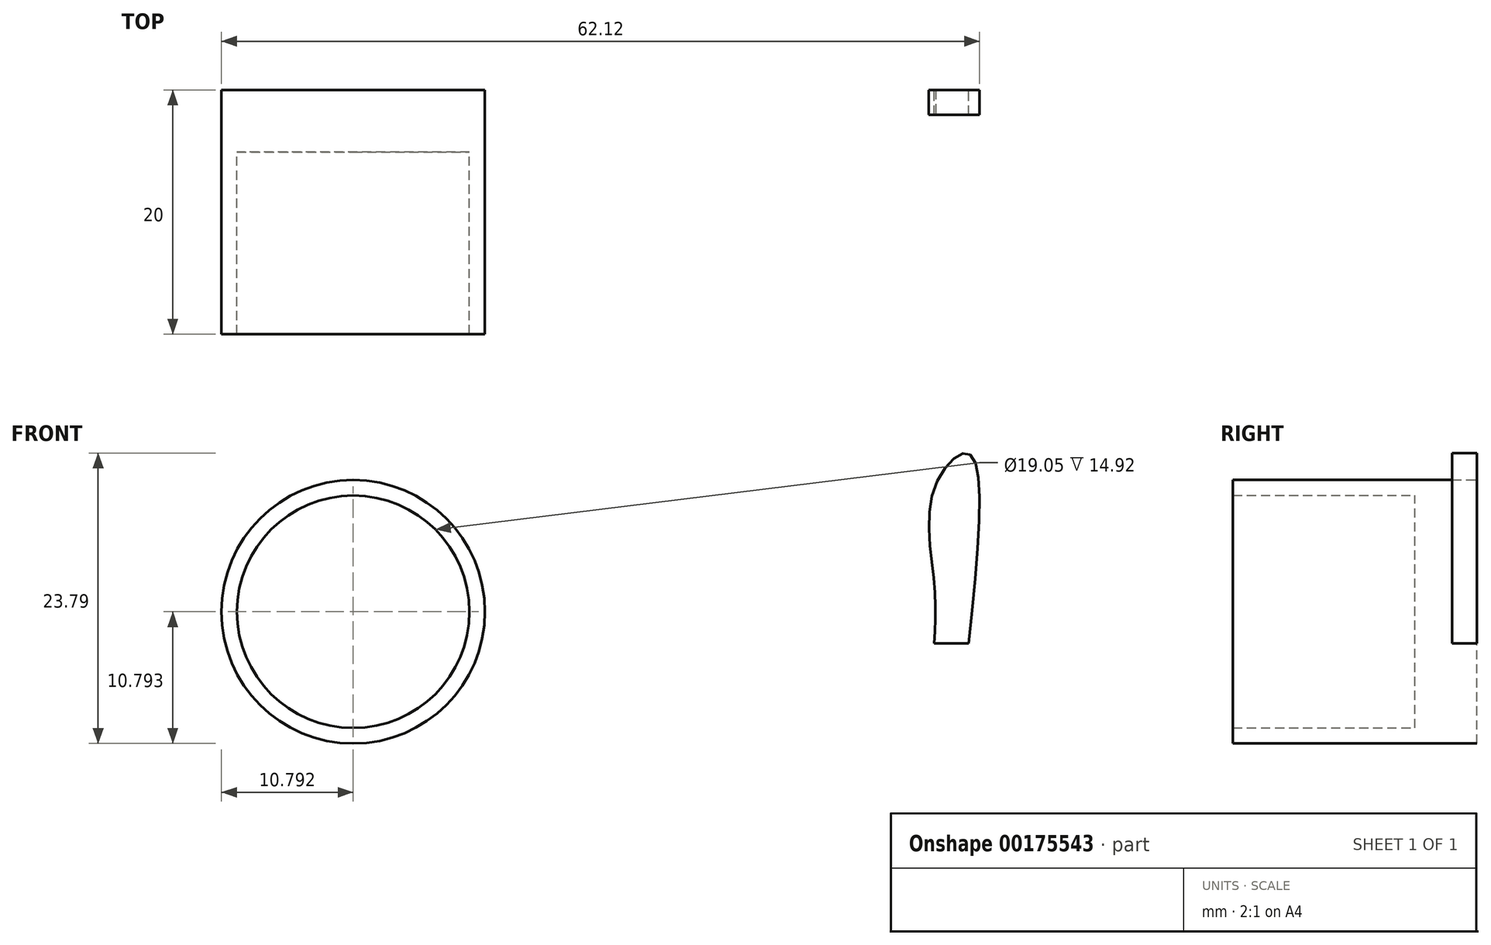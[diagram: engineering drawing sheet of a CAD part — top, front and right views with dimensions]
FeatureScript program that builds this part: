
annotation { "Feature Type Name" : "Feature", "Feature Type Description" : "" }
export const myFeature = defineFeature(function(context is Context, id is Id, definition is map)
    precondition{}
    {
        {
            var Q0;
            Q0=qCreatedBy(makeId("Front.planeOp"),FACE);
            var sketch = newSketch(context, id + "F0", { "sketchPlane" : qUnion([Q0])});
            skCircle(sketch, "E0", {"center": v(-33.09, 15.7) * mm, "radius": 10.8 * mm});
            skCircle(sketch, "E1", {"center": v(-33.09, 15.7) * mm, "radius": 9.52 * mm});
            skSolve(sketch);
        }
        {
            var Q0;
            Q0=makeQuery(id+"F0.imprint","IMPRINT",FACE,{"disambiguationData":[TD([[makeQuery(id+"F0.imprint","IMPRINT",EDGE,{"derivedFrom":sQuery(id+"F0.wireOp",EDGE,"E0")}),1.0]])]});
            extrude(context, id + "F1", {"entities" : qUnion([Q0]), "depth" : 20 * mm});
        }
        {
            var Q0;
            Q0=makeQuery(id+"F0.imprint","IMPRINT",FACE,{"disambiguationData":[TD([[makeQuery(id+"F0.imprint","IMPRINT",EDGE,{"derivedFrom":sQuery(id+"F0.wireOp",EDGE,"E1")}),1.0]])]});
            extrude(context, id + "F2", {"entities" : qUnion([Q0]), "operationType" : NewBodyOperationType.ADD, "depth" : 5.08 * mm});
        }
        {
            var Q0;
            Q0=qCreatedBy(makeId("Front.planeOp"),FACE);
            var sketch = newSketch(context, id + "F3", { "sketchPlane" : qUnion([Q0])});
            skLineSegment(sketch, "E2", {"start": v(14.53, 13.13) * mm, "end": v(17.34, 13.13) * mm});
            skFitSpline(sketch, "E3", {"points": [v(14.53, 13.13) * mm, v(14.53, 18.08) * mm, v(14.53, 25.84) * mm, v(17.34, 28.65) * mm, v(17.34, 13.13) * mm], "startDerivative": vector(1.32, 22.49) * mm, "endDerivative": vector(-6.53, -62.01) * mm});
            skLineSegment(sketch, "E4", {"start": v(28.24, 12.47) * mm, "end": v(31.05, 12.47) * mm});
            skFitSpline(sketch, "E5", {"points": [v(31.05, 12.47) * mm, v(31.05, 18.74) * mm, v(31.05, 28.65) * mm, v(28.73, 27) * mm, v(28.07, 17.75) * mm, v(28.24, 12.47) * mm], "startDerivative": vector(-1.65, 25.93) * mm, "endDerivative": vector(0.36, -25.68) * mm});
            skLineSegment(sketch, "E6", {"start": v(14.2, -20.9) * mm, "end": v(17, -20.9) * mm});
            skFitSpline(sketch, "E7", {"points": [v(17, -20.9) * mm, v(15.36, -12.8) * mm, v(15.2, -6.36) * mm, v(13.54, -3.55) * mm, v(12.88, -9.33) * mm, v(13.21, -16.93) * mm, v(14.2, -20.9) * mm], "startDerivative": vector(-11.62, 41.58) * mm, "endDerivative": vector(8.16, -26.34) * mm});
            skLineSegment(sketch, "E8", {"start": v(27.08, -21.06) * mm, "end": v(29.9, -21.06) * mm});
            skFitSpline(sketch, "E9", {"points": [v(27.08, -21.06) * mm, v(27.08, -14.45) * mm, v(28.4, -7.35) * mm, v(29.9, -4.05) * mm, v(29.9, -11.31) * mm, v(29.9, -21.06) * mm], "startDerivative": vector(-1.2, 33.16) * mm, "endDerivative": vector(0.94, -37.24) * mm});
            skSolve(sketch);
        }
        {
            var Q0;
            Q0=makeQuery(id+"F3.imprint","IMPRINT",FACE,{"disambiguationData":[TD([[makeQuery(id+"F3.imprint","IMPRINT",EDGE,{"derivedFrom":sQuery(id+"F3.wireOp",EDGE,"E2")}),1.0]])]});
            extrude(context, id + "F4", {"entities" : qUnion([Q0]), "depth" : 2.03 * mm});
        }
    });
